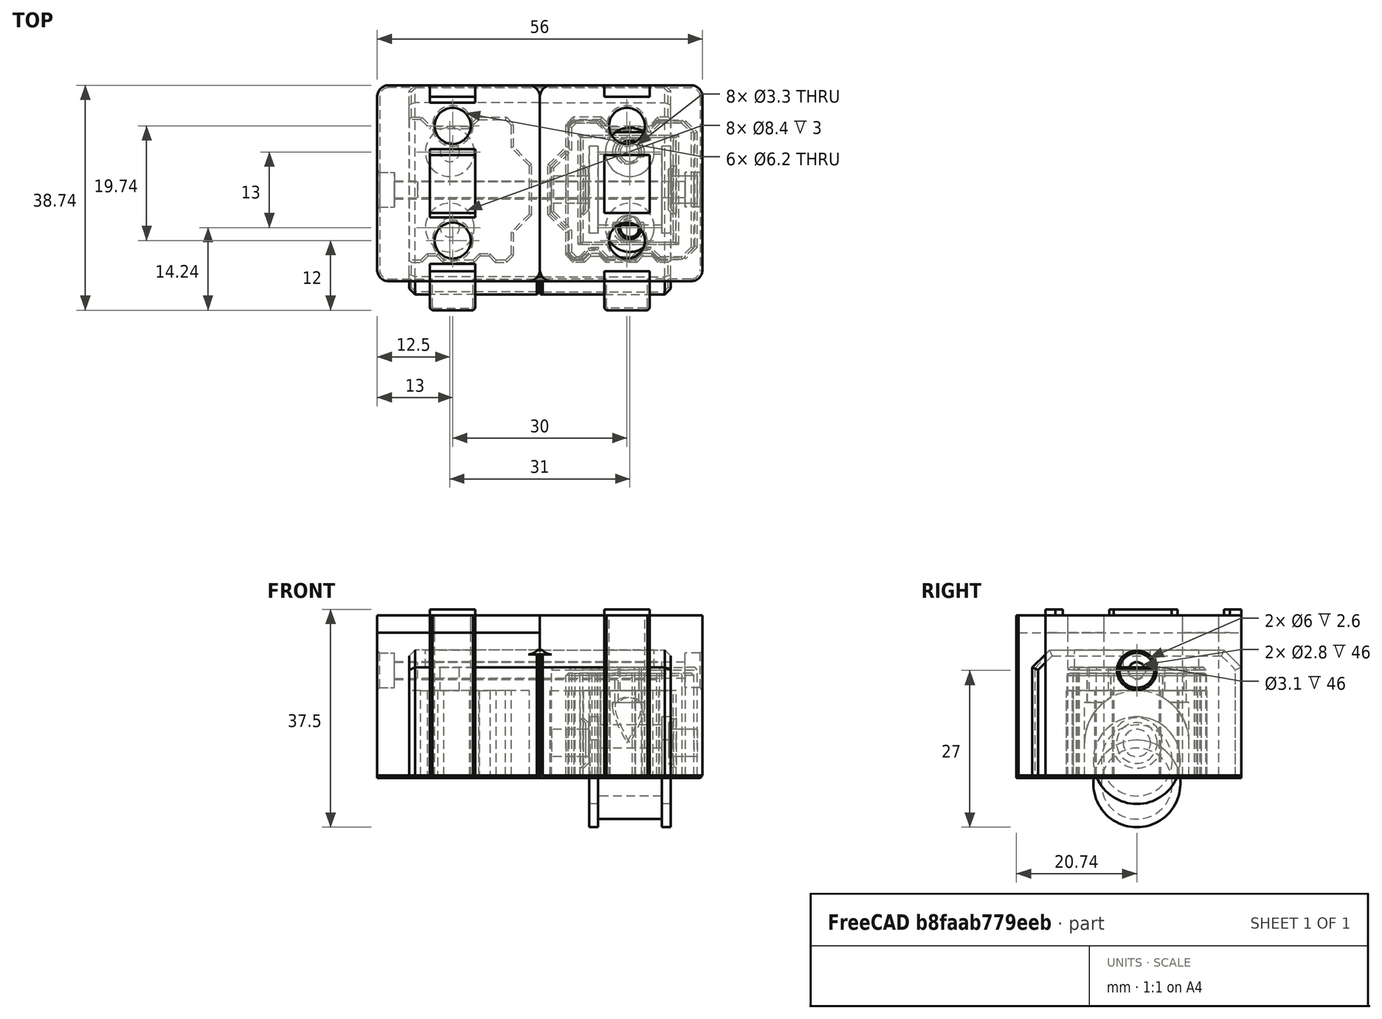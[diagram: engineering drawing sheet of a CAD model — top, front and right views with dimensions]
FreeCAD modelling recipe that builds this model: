
FCSTD DOCUMENT  (FreeCAD 0.19R24291 (Git))
Label: z-idler
License: All rights reserved
LicenseURL: http://en.wikipedia.org/wiki/All_rights_reserved
objects: Part::Box×24, Part::MultiFuse×22, Part::Cylinder×19, Part::Chamfer×14, Part::Cut×13, Part::Feature×8, Part::Refine×2, Part::MultiCommon×1, Part::Fillet×1, Part::Mirroring×1
note: 105 computed .brp shape members not serialized (recipe doc carries the construction recipe); baked Part::Feature solids carry a one-line shape summary decoded from their .brp

FEATURE [Part::Cylinder] Cylinder011
  Angle = 360
  AttacherType = Attacher::AttachEngine3D
  Height = 11
  Placement = pos=(5.5,0,1e-15) rot=(0,-1,0;1.5708rad)
  Radius = 6.11
FEATURE [Part::Cylinder] Cylinder012
  Angle = 360
  AttacherType = Attacher::AttachEngine3D
  Height = 1.5
  Placement = pos=(-5.5,0,3e-15) rot=(0,-1,0;1.5708rad)
  Radius = 7.5
FEATURE [Part::Cylinder] Cylinder013
  Angle = 360
  AttacherType = Attacher::AttachEngine3D
  Height = 1.5
  Placement = pos=(7,0,1e-15) rot=(0,-1,0;1.5708rad)
  Radius = 7.5
FEATURE [Part::MultiFuse] Fusion013005011003  label="20t-9mm-pulley"
  Placement = pos=(15.5,0,3) rot=(0,0,1;0rad)
  Shapes = -> [Cylinder013,Cylinder012,Cylinder011]
FEATURE [Part::Box] Box011  label="Cube011"
  AttacherType = Attacher::AttachEngine3D
  Height = 6
  Length = 16
  Placement = pos=(7,-9,0) rot=(0,0,1;0rad)
  Width = 18
FEATURE [Part::Cylinder] Cylinder014
  Angle = 360
  AttacherType = Attacher::AttachEngine3D
  Height = 16
  Placement = pos=(23,0,6) rot=(0,-1,0;1.5708rad)
  Radius = 9
FEATURE [Part::Cylinder] Cylinder015
  Angle = 360
  AttacherType = Attacher::AttachEngine3D
  Height = 33
  Placement = pos=(31,0,6) rot=(0,-1,0;1.5708rad)
  Radius = 2.35
FEATURE [Part::MultiFuse] Fusion013005011004
  Shapes = -> [Cylinder014,Box011]
FEATURE [Part::Box] Box012  label="Cube012"
  AttacherType = Attacher::AttachEngine3D
  Height = 19
  Length = 22
  Placement = pos=(4.6,-11.9,0) rot=(0,0,1;0rad)
  Width = 23.8
FEATURE [Part::Cylinder] Cylinder016
  Angle = 360
  AttacherType = Attacher::AttachEngine3D
  Height = 1
  Placement = pos=(23.15,0,6) rot=(0,-1,0;1.5708rad)
  Radius = 4.35
FEATURE [Part::Cylinder] Cylinder017
  Angle = 360
  AttacherType = Attacher::AttachEngine3D
  Height = 1
  Placement = pos=(7.85,0,6) rot=(0,-1,0;1.5708rad)
  Radius = 4.35
FEATURE [Part::MultiFuse] Fusion013005011005
  Shapes = -> [Cylinder017,Cylinder016]
FEATURE [Part::Chamfer] Chamfer003036
  Base = -> Fusion013005011005
  Edges = 2 edges r=0.85: [Edge3,Edge4]
FEATURE [Part::Box] Box013  label="Cube013"
  AttacherType = Attacher::AttachEngine3D
  Height = 22
  Length = 10.2
  Placement = pos=(9.9,10.3,0) rot=(0,0,1;0rad)
  Width = 10
FEATURE [Part::Box] Box014  label="Cube014"
  AttacherType = Attacher::AttachEngine3D
  Height = 22
  Length = 4.2
  Placement = pos=(6.9,-20.3,0) rot=(0,0,1;0rad)
  Width = 10
FEATURE [Part::Box] Box015  label="Cube015"
  AttacherType = Attacher::AttachEngine3D
  Height = 18
  Length = 22.2
  Placement = pos=(4.4,-12.1,0) rot=(0,0,1;0rad)
  Width = 24.2
FEATURE [Part::Cylinder] Cylinder018
  Angle = 360
  AttacherType = Attacher::AttachEngine3D
  Height = 10
  Placement = pos=(15,-6.5,13) rot=(0,0,1;0rad)
  Radius = 2
FEATURE [Part::Cylinder] Cylinder019
  Angle = 360
  AttacherType = Attacher::AttachEngine3D
  Height = 10
  Placement = pos=(15,6.5,13) rot=(0,0,1;0rad)
  Radius = 2
FEATURE [Part::Cylinder] Cylinder020
  Angle = 360
  AttacherType = Attacher::AttachEngine3D
  Height = 10
  Placement = pos=(15,-6.5,3) rot=(0,0,1;0rad)
  Radius = 2.5
FEATURE [Part::Cylinder] Cylinder021
  Angle = 360
  AttacherType = Attacher::AttachEngine3D
  Height = 10
  Placement = pos=(15,6.5,3) rot=(0,0,1;0rad)
  Radius = 2.5
FEATURE [Part::Chamfer] Chamfer003042
  Base = -> Box015
  Edges = 2 edges r=1: [Edge1,Edge3]
  Placement = pos=(0.5,0,-3) rot=(0,0,1;0rad)
FEATURE [Part::Box] Box018  label="Cube018"
  AttacherType = Attacher::AttachEngine3D
  Height = 22
  Length = 22.5
  Placement = pos=(0,-18,0) rot=(0,0,1;0rad)
  Width = 36
FEATURE [Part::Box] Box021  label="Cube021"
  AttacherType = Attacher::AttachEngine3D
  Height = 15
  Length = 10
  Placement = pos=(10,10.5,0) rot=(0,0,1;0rad)
  Width = 3
FEATURE [Part::Box] Box022  label="Cube022"
  AttacherType = Attacher::AttachEngine3D
  Height = 15
  Length = 4
  Placement = pos=(7,-13.5,0) rot=(0,0,1;0rad)
  Width = 3
FEATURE [Part::Cylinder] Cylinder022
  Angle = 360
  AttacherType = Attacher::AttachEngine3D
  Height = 3
  Placement = pos=(15.5,6.5,19) rot=(0,0,1;0rad)
  Radius = 4.2
FEATURE [Part::Cylinder] Cylinder023
  Angle = 360
  AttacherType = Attacher::AttachEngine3D
  Height = 3
  Placement = pos=(15.5,-6.5,19) rot=(0,0,1;0rad)
  Radius = 4.2
FEATURE [Part::Cylinder] Cylinder024
  Angle = 360
  AttacherType = Attacher::AttachEngine3D
  Height = 10
  Placement = pos=(15,6.5,12) rot=(0,0,1;0rad)
  Radius = 1.65
FEATURE [Part::Cylinder] Cylinder025
  Angle = 360
  AttacherType = Attacher::AttachEngine3D
  Height = 10
  Placement = pos=(15,-6.5,12) rot=(0,0,1;0rad)
  Radius = 1.65
FEATURE [Part::MultiFuse] Fusion013005011016
  Placement = pos=(0.5,0,0) rot=(0,0,1;0rad)
  Shapes = -> [Cylinder025,Cylinder024]
FEATURE [Part::Box] Box025  label="Cube023"
  AttacherType = Attacher::AttachEngine3D
  Height = 22
  Length = 4.2
  Placement = pos=(15.9,-20.3,0) rot=(0,0,1;0rad)
  Width = 10
FEATURE [Part::Box] Box026  label="Cube024"
  AttacherType = Attacher::AttachEngine3D
  Height = 15
  Length = 4
  Placement = pos=(16,-13.5,0) rot=(0,0,1;0rad)
  Width = 3
FEATURE [Part::MultiFuse] Fusion013005011025
  Shapes = -> [Box026,Box021,Box022]
FEATURE [Part::Chamfer] Chamfer003060
  Base = -> Fusion013005011025
  Edges = 6 edges r=1.6: [Edge3,Edge7,Edge13,Edge17,Edge27,Edge31]
FEATURE [Part::Box] Box027  label="Cube025"
  AttacherType = Attacher::AttachEngine3D
  Height = 19
  Length = 13
  Placement = pos=(6,-11,0) rot=(0,0,1;0rad)
  Width = 10
FEATURE [Part::Cut] Cut001001032
  Base = -> Chamfer003060
  Placement = pos=(0.5,0,0) rot=(0,0,1;0rad)
  Tool = -> Box027
FEATURE [Part::Cut] Cut
  Base = -> Box018
  Tool = -> Chamfer003042
FEATURE [Part::MultiFuse] Fusion
  Shapes = -> [Cut,Cut001001032]
FEATURE [Part::Chamfer] Chamfer
  Base = -> Fusion
  Edges = 2 edges r=3: [Edge7,Edge8]
FEATURE [Part::Chamfer] Chamfer003061
  Base = -> Chamfer
  Edges = 5 edges r=1: [Edge7,Edge11,Edge33,Edge34,Edge36]
FEATURE [Part::Box] Box  label="Cube"
  AttacherType = Attacher::AttachEngine3D
  Height = 28
  Length = 28
  Placement = pos=(-28,-18,0) rot=(0,0,1;0rad)
  Width = 36
FEATURE [Part::MultiFuse] Fusion013005011026
  Shapes = -> [Cylinder022,Cylinder023]
FEATURE [Part::MultiFuse] Fusion013005011027
  Shapes = -> [Fusion013005011026,Fusion013005011016]
FEATURE [Part::Cut] Cut001001033
  Base = -> Chamfer003061
  Tool = -> Fusion013005011027
FEATURE [Part::Box] Box029  label="Cube027"
  AttacherType = Attacher::AttachEngine3D
  Height = 22
  Length = 3
  Placement = pos=(-2,-18,0) rot=(0,0,1;0rad)
  Width = 36
FEATURE [Part::Chamfer] Chamfer003062
  Base = -> Box029
  Edges = 2 edges r=3: [Edge10,Edge12]
FEATURE [Part::Box] Box030  label="Cube028"
  AttacherType = Attacher::AttachEngine3D
  Height = 1
  Length = 7.8
  Placement = pos=(-18.9,-15.74,25) rot=(0,0,1;0rad)
  Width = 3
FEATURE [Part::Cylinder] Cylinder
  Angle = 360
  AttacherType = Attacher::AttachEngine3D
  Height = 32
  Placement = pos=(-15,11,0) rot=(0,0,1;0rad)
  Radius = 3.1
FEATURE [Part::Cylinder] Cylinder026
  Angle = 360
  AttacherType = Attacher::AttachEngine3D
  Height = 32
  Placement = pos=(-15,-8.74,0) rot=(0,0,1;0rad)
  Radius = 3.1
FEATURE [Part::Box] Box031  label="Cube029"
  AttacherType = Attacher::AttachEngine3D
  Height = 1
  Length = 7.8
  Placement = pos=(-18.9,-4.74,25) rot=(0,0,1;0rad)
  Width = 11.74
FEATURE [Part::Box] Box032  label="Cube030"
  AttacherType = Attacher::AttachEngine3D
  Height = 1
  Length = 7.8
  Placement = pos=(-18.9,15,25) rot=(0,0,1;0rad)
  Width = 3
FEATURE [Part::Cylinder] Cylinder027
  Angle = 360
  AttacherType = Attacher::AttachEngine3D
  Height = 46
  Placement = pos=(-25,0,18.5) rot=(0,1,0;1.5708rad)
  Radius = 1.4
FEATURE [Part::Cylinder] Cylinder028
  Angle = 360
  AttacherType = Attacher::AttachEngine3D
  Height = 4
  Placement = pos=(-29,0,18.5) rot=(0,1,0;1.5708rad)
  Radius = 3
FEATURE [Part::Box] Box033  label="Cube031"
  AttacherType = Attacher::AttachEngine3D
  Height = 30
  Length = 60
  Placement = pos=(-31.48,-25.74,0) rot=(0,0,1;0rad)
  Width = 10
FEATURE [Part::Box] Box034  label="Cube032"
  AttacherType = Attacher::AttachEngine3D
  Height = 28
  Length = 10
  Placement = pos=(-9.9,-25.74,0) rot=(0,0,1;0rad)
  Width = 10
FEATURE [Part::MultiFuse] Fusion013005011029005
  Shapes = -> [Chamfer003062,Cut001001033]
FEATURE [Part::Cut] Cut001001035
  Base = -> Fusion013005011029005
  Tool = -> Box034
FEATURE [Part::Feature] Fusion013005011029006001  label="Fusion013005011029007"
  shape: bbox 50.5 x 36 x 25 mm, 45 faces (baked)
FEATURE [Part::Feature] Fusion013005011003001  label="20t-9mm-pulley001"
  shape: bbox 14 x 15 x 15 mm, 7 faces (baked)
FEATURE [Part::MultiFuse] Fusion013005011029006002
  Shapes = -> [Fusion013005011003001,Fusion013005011029006001]
FEATURE [Part::Box] Box035  label="Cube033"
  AttacherType = Attacher::AttachEngine3D
  Height = 28
  Length = 7.8
  Placement = pos=(-18.9,-20.74,0) rot=(0,0,1;0rad)
  Width = 6
FEATURE [Part::MultiFuse] Fusion013005011029006004
  Placement = pos=(0,0,3) rot=(0,0,1;0rad)
  Shapes = -> [Box030,Box031,Box032]
FEATURE [Part::MultiFuse] Fusion013005011029006006
  Shapes = -> [Cylinder,Cylinder026]
FEATURE [Part::Feature] Cut001001036001  label="Cut001001037"
  shape: bbox 50.5 x 38.74 x 25 mm, 55 faces (baked)
FEATURE [Part::Feature] Chamfer003068001  label="idler-housing001"
  shape: bbox 22 x 24 x 18 mm, 96 faces (baked)
FEATURE [Part::Box] Box036  label="Cube034"
  AttacherType = Attacher::AttachEngine3D
  Height = 10
  Length = 33
  Placement = pos=(-30,-23,22) rot=(0,0,1;0rad)
  Width = 47
FEATURE [Part::Feature] Chamfer003065001
  shape: bbox 50.5 x 38.74 x 26 mm, 117 faces (baked)
FEATURE [Part::MultiCommon] Common
  Placement = pos=(0,0,3) rot=(0,0,1;0rad)
  Shapes = -> [Chamfer003065001,Box036]
FEATURE [Part::MultiFuse] Fusion013005011029006008001002
  Shapes = -> [Box013,Box014,Box025]
FEATURE [Part::Chamfer] Chamfer003068003
  Base = -> Fusion013005011029006008001002
  Edges = 6 edges r=1.6: [Edge1,Edge5,Edge15,Edge19,Edge27,Edge31]
FEATURE [Part::MultiFuse] Fusion013005011029006008001003
  Shapes = -> [Cylinder018,Cylinder019]
FEATURE [Part::MultiFuse] Fusion013005011029006008001004
  Shapes = -> [Cylinder020,Cylinder021]
FEATURE [Part::MultiFuse] Fusion013005011029006008001005
  Shapes = -> [Cylinder020,Cylinder021,Fusion013005011029006008001003,Fusion013005011029006008001004]
FEATURE [Part::Cut] Cut001001036003
  Base = -> Box012
  Tool = -> Chamfer003068003
FEATURE [Part::Cut] Cut001001036004
  Base = -> Cut001001036003
  Tool = -> Fusion013005011004
FEATURE [Part::Cut] Cut001001036005
  Base = -> Cut001001036004
  Tool = -> Fusion013005011029006008001005
FEATURE [Part::MultiFuse] Fusion013005011029006008001006
  Shapes = -> [Cut001001036005,Chamfer003036]
FEATURE [Part::Chamfer] Chamfer003068004
  Base = -> Fusion013005011029006008001006
  Edges = 2 edges r=1: [Edge1,Edge3]
FEATURE [Part::Chamfer] Chamfer003068005
  Base = -> Chamfer003068004
  Edges = 2 edges r=2: [Edge56,Edge58]
  Placement = pos=(0.5,0,0) rot=(0,0,1;0rad)
FEATURE [Part::Box] Box037  label="Cube035"
  AttacherType = Attacher::AttachEngine3D
  Height = 19
  Length = 5
  Placement = pos=(2,-7,0) rot=(0,0,1;0rad)
  Width = 14
FEATURE [Part::Box] Box038  label="Cube036"
  AttacherType = Attacher::AttachEngine3D
  Height = 15
  Length = 4
  Placement = pos=(1.8,-7.25,0) rot=(0,0,1;0rad)
  Width = 14.5
FEATURE [Part::Cut] Cut001001036007
  Base = -> Box
  Tool = -> Box033
FEATURE [Part::Fillet] Fillet
  Base = -> Cut001001036007
  Edges = 4 edges r=2: [Edge2,Edge4,Edge9,Edge12]
FEATURE [Part::Chamfer] Chamfer003068008
  Base = -> Box035
  Edges = 2 edges r=0.4: [Edge1,Edge5]
FEATURE [Part::MultiFuse] Fusion013005011029006008001007
  Shapes = -> [Fillet,Chamfer003068008,Fusion013005011029006004]
FEATURE [Part::Chamfer] Chamfer003068009
  Base = -> Box038
  Edges = 2 edges r=3.1: [Edge1,Edge3]
FEATURE [Part::Cut] Cut001001036008
  Base = -> Cut001001035
  Tool = -> Chamfer003068009
FEATURE [Part::MultiFuse] Fusion013005011029006008001008
  Shapes = -> [Cut001001036008,Fusion013005011029006008001007]
FEATURE [Part::Cut] Cut001001036009
  Base = -> Fusion013005011029006008001008
  Tool = -> Fusion013005011029006006
FEATURE [Part::Chamfer] Chamfer003068011
  Base = -> Box037
  Edges = 2 edges r=3.1: [Edge1,Edge3]
FEATURE [Part::MultiFuse] Fusion013005011029006008001009
  Shapes = -> [Chamfer003068011,Chamfer003068005]
FEATURE [Part::Cut] Cut001001036010002
  Base = -> Fusion013005011029006008001009
  Tool = -> Cylinder015
FEATURE [Part::Refine] Cut001001036010002001
  Source = -> Cut001001036010002
FEATURE [Part::Chamfer] Chamfer003068012
  Base = -> Cut001001036010002001
  Edges = 52 edges r=0.4: [Edge7,Edge10,Edge12,Edge13,Edge15,Edge16,Edge20,Edge21,Edge23,Edge25,Edge27,Edge28,Edge30,Edge31,Edge37,Edge38,Edge40,Edge42,Edge44,Edge46,Edge47,Edge48,Edge50,Edge51,Edge53,Edge54,Edge56,Edge58,Edge59,Edge60,Edge62,Edge63,Edge64,Edge65,Edge67,Edge69,Edge70,Edge72,Edge73,Edge74,Edge76,Edge77,Edge79,+9 more]
FEATURE [Part::Feature] Chamfer003068012001
  shape: bbox 25.1 x 23.8 x 19 mm, 95 faces (baked)
FEATURE [Part::MultiFuse] Fusion013005011029006008001010
  Shapes = -> [Cylinder028,Cylinder027]
FEATURE [Part::Cut] Cut001001036010002002
  Base = -> Cut001001036009
  Tool = -> Fusion013005011029006008001010
FEATURE [Part::Refine] Cut001001036010002002001
  Source = -> Cut001001036010002002
FEATURE [Part::Chamfer] Chamfer003068012002
  Base = -> Cut001001036010002002001
  Edges = 43 edges r=0.4: [Edge4,Edge5,Edge9,Edge11,Edge16,Edge17,Edge21,Edge23,Edge28,Edge29,Edge32,Edge35,Edge38,Edge46,Edge50,Edge53,Edge54,Edge57,Edge65,Edge67,Edge70,Edge76,Edge77,Edge79,Edge82,Edge84,Edge85,Edge86,Edge87,Edge88,Edge89,Edge90,Edge91,Edge92,Edge93,Edge94,Edge95,Edge96,Edge97,Edge98,Edge99,Edge100,Edge105]
FEATURE [Part::Box] Box039  label="Cube037"
  AttacherType = Attacher::AttachEngine3D
  Height = 10
  Length = 10
  Placement = pos=(-20,6,28) rot=(0,0,1;0rad)
  Width = 10
FEATURE [Part::Box] Box040  label="Cube038"
  AttacherType = Attacher::AttachEngine3D
  Height = 10
  Length = 10
  Placement = pos=(-20,-14,28) rot=(0,0,1;0rad)
  Width = 10
FEATURE [Part::MultiFuse] Fusion013005011029006008001011
  Shapes = -> [Box040,Box039]
FEATURE [Part::Cut] Cut001001036010002002002
  Base = -> Chamfer003068012002
  Tool = -> Fusion013005011029006008001011
FEATURE [Part::Feature] Cut001001036010002002002001001
  shape: bbox 50.5 x 38.74 x 29 mm, 120 faces (baked)
FEATURE [Part::Mirroring] Part__Mirroring  label="Cut001001036010002002002001001 (Mirror #1)"
  Base = (0,0,0)
  Normal = (1,0,0)
  Source = -> Cut001001036010002002002001001
FEATURE [Part::Feature] Part__Mirroring001  label="Cut001001036010002002002001001 (Mirror #1)001"
  shape: bbox 50.5 x 38.74 x 29 mm, 120 faces (baked)
